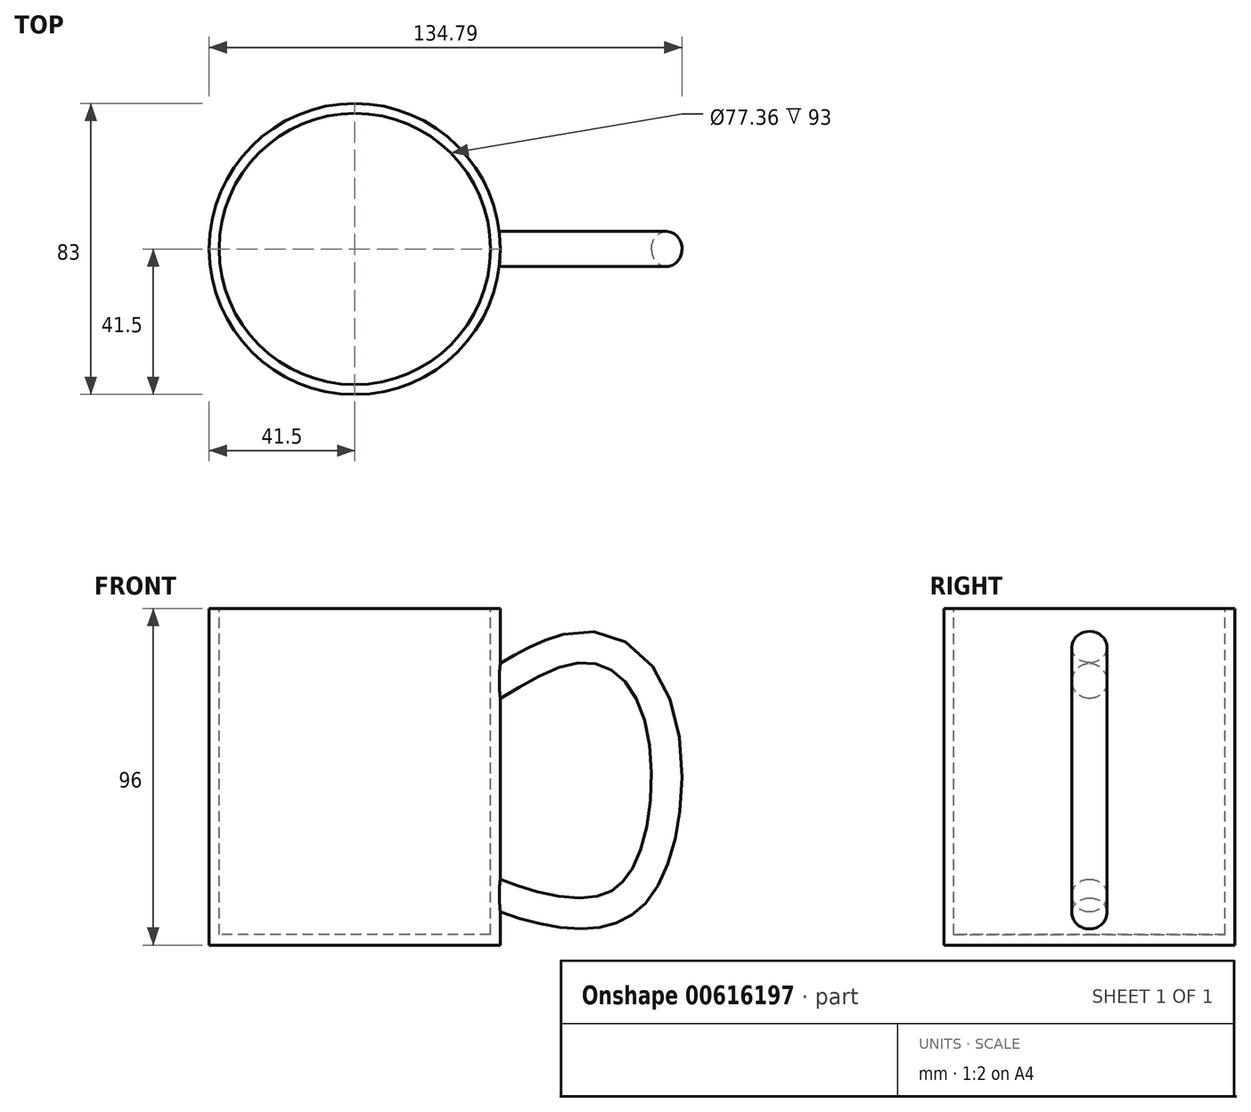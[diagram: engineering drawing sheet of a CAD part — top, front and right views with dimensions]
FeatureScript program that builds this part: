
annotation { "Feature Type Name" : "Feature", "Feature Type Description" : "" }
export const myFeature = defineFeature(function(context is Context, id is Id, definition is map)
    precondition{}
    {
        {
            var Q0;
            Q0=qCreatedBy(makeId("Top.planeOp"),FACE);
            var sketch = newSketch(context, id + "F0", { "sketchPlane" : qUnion([Q0])});
            skCircle(sketch, "E0", {"center": v(0, 0) * mm, "radius": 41.5 * mm});
            skSolve(sketch);
        }
        {
            var Q0;
            Q0 = qSketchRegion(id + "F0", true);
            var Q1;
            Q1=makeQuery(id+"F0.imprint","IMPRINT",FACE,{"disambiguationData":[TD([[makeQuery(id+"F0.imprint","IMPRINT",EDGE,{"derivedFrom":sQuery(id+"F0.wireOp",EDGE,"E0")}),1.0]])]});
            extrude(context, id + "F1", {"entities" : qUnion([Q0, Q1]), "depth" : 96 * mm, "offsetDistance" : 25 * mm});
        }
        {
            var Q0;
            Q0=qCreatedBy(makeId("Front.planeOp"),FACE);
            var sketch = newSketch(context, id + "F2", { "sketchPlane" : qUnion([Q0])});
            skFitSpline(sketch, "E1", {"points": [v(36.86, 70.02) * mm, v(63.87, 82.38) * mm, v(83.65, 67.15) * mm, v(80.95, 21.25) * mm, v(63.44, 11.55) * mm, v(36.88, 19) * mm], "startDerivative": vector(76.68, 34.6) * mm, "endDerivative": vector(-74.32, 45.68) * mm});
            skSolve(sketch);
        }
        {
            var Q0;
            Q0=qCreatedBy(makeId("Right.planeOp"),FACE);
            cPlane(context, id + "F3", {"entities" : qUnion([Q0]), "cplaneType" : CPlaneType.OFFSET, "offset" : 42 * mm, "width" : 150 * mm, "height" : 150 * mm});
        }
        {
            var Q0;
            Q0=qCreatedBy(id+"F3.planeOp",FACE);
            var sketch = newSketch(context, id + "F4", { "sketchPlane" : qUnion([Q0])});
            skCircle(sketch, "E2", {"center": v(0, 75.66) * mm, "radius": 5 * mm});
            skSolve(sketch);
        }
        {
            var Q0;
            Q0=makeQuery(id+"F4.imprint","IMPRINT",FACE,{"disambiguationData":[TD([[makeQuery(id+"F4.imprint","IMPRINT",EDGE,{"derivedFrom":sQuery(id+"F4.wireOp",EDGE,"E2")}),1.0]])]});
            var Q1;
            Q1=sQuery(id+"F4.wireOp",EDGE,"E2");
            var Q2;
            Q2=sQuery(id+"F2.wireOp",EDGE,"E1");
            sweep(context, id + "F5", {"operationType" : NewBodyOperationType.ADD, "profiles" : qUnion([Q0]), "surfaceProfiles" : qUnion([Q1]), "path" : qUnion([Q2])});
        }
        {
            var Q0;
            Q0=makeQuery(id+"F1.opExtrude","CAP_FACE",FACE,{"disambiguationData":[OSD([sQuery(id+"F0.wireOp",EDGE,"E0")])],"isStart":false});
            var sketch = newSketch(context, id + "F6", { "sketchPlane" : qUnion([Q0])});
            skCircle(sketch, "E3", {"center": v(0, 0) * mm, "radius": 38.68 * mm});
            skSolve(sketch);
        }
        {
            var Q0;
            Q0 = qSketchRegion(id + "F6", true);
            extrude(context, id + "F7", {"entities" : qUnion([Q0]), "operationType" : NewBodyOperationType.REMOVE, "oppositeDirection" : true, "depth" : 93 * mm, "offsetDistance" : 25 * mm});
        }
    });
